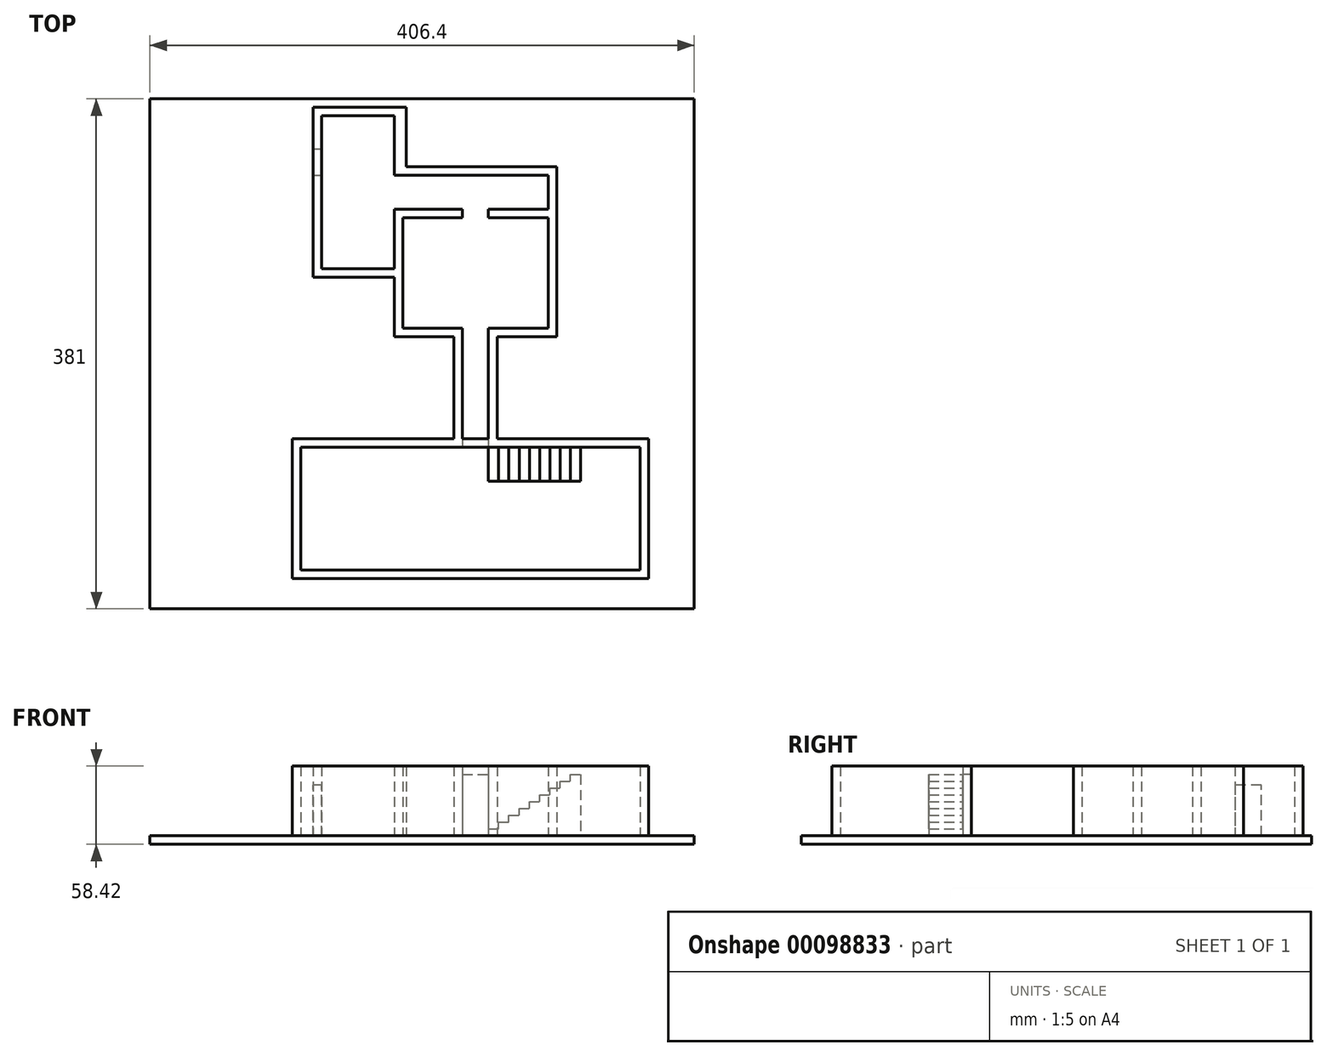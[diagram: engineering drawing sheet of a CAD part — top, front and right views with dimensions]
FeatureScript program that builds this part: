
annotation { "Feature Type Name" : "Feature", "Feature Type Description" : "" }
export const myFeature = defineFeature(function(context is Context, id is Id, definition is map)
    precondition{}
    {
        {
            var Q0;
            Q0=qCreatedBy(makeId("Top.planeOp"),FACE);
            var sketch = newSketch(context, id + "F0", { "sketchPlane" : qUnion([Q0])});
            skLineSegment(sketch, "E0.bottom", {"start": v(-211.11, 667.88) * mm, "end": v(195.29, 667.88) * mm});
            skLineSegment(sketch, "E0.top", {"start": v(-211.11, 286.88) * mm, "end": v(195.29, 286.88) * mm});
            skLineSegment(sketch, "E0.left", {"start": v(-211.11, 667.88) * mm, "end": v(-211.11, 286.88) * mm});
            skLineSegment(sketch, "E0.right", {"start": v(195.29, 667.88) * mm, "end": v(195.29, 286.88) * mm});
            skSolve(sketch);
        }
        {
            var Q0;
            Q0 = qSketchRegion(id + "F0", true);
            extrude(context, id + "F1", {"entities" : qUnion([Q0]), "oppositeDirection" : true, "depth" : 6.35 * mm});
        }
        {
            var Q0;
            Q0=makeQuery(id+"F1.opExtrude","CAP_FACE",FACE,{"disambiguationData":[OSD([sQuery(id+"F0.wireOp",EDGE,"E0.bottom"),sQuery(id+"F0.wireOp",EDGE,"E0.top"),sQuery(id+"F0.wireOp",EDGE,"E0.left"),sQuery(id+"F0.wireOp",EDGE,"E0.right")])],"isStart":true});
            var sketch = newSketch(context, id + "F2", { "sketchPlane" : qUnion([Q0])});
            skLineSegment(sketch, "E1", {"start": v(-89.15, 534.53) * mm, "end": v(-89.15, 661.53) * mm});
            skLineSegment(sketch, "E2", {"start": v(-89.15, 661.53) * mm, "end": v(-19.87, 661.53) * mm});
            skLineSegment(sketch, "E3", {"start": v(-28.62, 585.33) * mm, "end": v(-28.62, 540.88) * mm});
            skLineSegment(sketch, "E4", {"start": v(-28.62, 540.88) * mm, "end": v(-82.8, 540.88) * mm});
            skLineSegment(sketch, "E5", {"start": v(-82.8, 540.88) * mm, "end": v(-82.8, 655.18) * mm});
            skLineSegment(sketch, "E6", {"start": v(-82.8, 655.18) * mm, "end": v(-28.62, 655.18) * mm});
            skLineSegment(sketch, "E7", {"start": v(-28.62, 655.18) * mm, "end": v(-28.62, 610.73) * mm});
            skLineSegment(sketch, "E8", {"start": v(22.18, 585.33) * mm, "end": v(-28.62, 585.33) * mm});
            skLineSegment(sketch, "E9", {"start": v(-89.15, 534.53) * mm, "end": v(-28.62, 534.53) * mm});
            skLineSegment(sketch, "E10", {"start": v(-28.62, 534.53) * mm, "end": v(-28.62, 490.05) * mm});
            skLineSegment(sketch, "E11", {"start": v(-22.27, 496.4) * mm, "end": v(-22.27, 578.98) * mm});
            skLineSegment(sketch, "E12", {"start": v(-22.27, 578.98) * mm, "end": v(22.18, 578.98) * mm});
            skLineSegment(sketch, "E13", {"start": v(22.18, 578.98) * mm, "end": v(22.18, 585.33) * mm});
            skLineSegment(sketch, "E14", {"start": v(-19.87, 661.53) * mm, "end": v(-19.87, 617.08) * mm});
            skLineSegment(sketch, "E15", {"start": v(41.7, 578.98) * mm, "end": v(41.7, 585.33) * mm});
            skLineSegment(sketch, "E16", {"start": v(92.5, 585.33) * mm, "end": v(92.5, 490.05) * mm});
            skLineSegment(sketch, "E17", {"start": v(86.16, 496.41) * mm, "end": v(86.16, 578.98) * mm});
            skLineSegment(sketch, "E18", {"start": v(86.16, 578.98) * mm, "end": v(41.7, 578.98) * mm});
            skLineSegment(sketch, "E19", {"start": v(92.5, 617.08) * mm, "end": v(-19.87, 617.08) * mm});
            skLineSegment(sketch, "E20", {"start": v(92.5, 610.73) * mm, "end": v(92.5, 585.33) * mm});
            skLineSegment(sketch, "E21", {"start": v(92.5, 617.08) * mm, "end": v(92.5, 610.73) * mm});
            skLineSegment(sketch, "E22", {"start": v(86.16, 610.73) * mm, "end": v(86.16, 585.33) * mm});
            skLineSegment(sketch, "E23", {"start": v(86.16, 585.33) * mm, "end": v(41.7, 585.33) * mm});
            skLineSegment(sketch, "E24", {"start": v(86.16, 610.73) * mm, "end": v(-28.62, 610.73) * mm});
            skLineSegment(sketch, "E25", {"start": v(22.18, 490.05) * mm, "end": v(22.18, 496.4) * mm});
            skLineSegment(sketch, "E26", {"start": v(22.18, 496.4) * mm, "end": v(-22.27, 496.4) * mm});
            skLineSegment(sketch, "E27", {"start": v(86.16, 496.41) * mm, "end": v(41.7, 496.41) * mm});
            skLineSegment(sketch, "E28", {"start": v(41.7, 496.41) * mm, "end": v(41.7, 490.05) * mm});
            skLineSegment(sketch, "E29", {"start": v(15.83, 490.05) * mm, "end": v(15.83, 413.85) * mm});
            skLineSegment(sketch, "E30", {"start": v(-28.62, 490.05) * mm, "end": v(15.83, 490.05) * mm});
            skLineSegment(sketch, "E31", {"start": v(48.06, 413.85) * mm, "end": v(48.06, 490.05) * mm});
            skLineSegment(sketch, "E32", {"start": v(48.06, 490.05) * mm, "end": v(92.5, 490.05) * mm});
            skLineSegment(sketch, "E33", {"start": v(22.18, 490.05) * mm, "end": v(22.18, 407.5) * mm});
            skLineSegment(sketch, "E34", {"start": v(41.7, 490.05) * mm, "end": v(41.7, 407.5) * mm});
            skLineSegment(sketch, "E35", {"start": v(41.7, 407.5) * mm, "end": v(154.83, 407.5) * mm});
            skLineSegment(sketch, "E36", {"start": v(154.83, 407.5) * mm, "end": v(154.83, 315.97) * mm});
            skLineSegment(sketch, "E37", {"start": v(154.83, 315.97) * mm, "end": v(-98.59, 315.97) * mm});
            skLineSegment(sketch, "E38", {"start": v(-98.59, 315.97) * mm, "end": v(-98.59, 407.5) * mm});
            skLineSegment(sketch, "E39", {"start": v(-98.59, 407.5) * mm, "end": v(22.18, 407.5) * mm});
            skLineSegment(sketch, "E40", {"start": v(15.83, 413.85) * mm, "end": v(-104.94, 413.85) * mm});
            skLineSegment(sketch, "E41", {"start": v(-104.94, 413.85) * mm, "end": v(-104.94, 309.62) * mm});
            skLineSegment(sketch, "E42", {"start": v(-104.94, 309.62) * mm, "end": v(161.18, 309.62) * mm});
            skLineSegment(sketch, "E43", {"start": v(161.18, 309.62) * mm, "end": v(161.18, 413.85) * mm});
            skLineSegment(sketch, "E44", {"start": v(161.18, 413.85) * mm, "end": v(48.06, 413.85) * mm});
            skSolve(sketch);
        }
        {
            var Q0;
            Q0 = qSketchRegion(id + "F2", true);
            extrude(context, id + "F3", {"entities" : qUnion([Q0]), "operationType" : NewBodyOperationType.ADD, "depth" : 52.07 * mm});
        }
        {
            var Q0;
            Q0=makeQuery(id+"F3.opExtrude","SWEPT_FACE",FACE,{"disambiguationData":[OSD([sQuery(id+"F2.wireOp",EDGE,"E1")])]});
            var sketch = newSketch(context, id + "F4", { "sketchPlane" : qUnion([Q0])});
            skLineSegment(sketch, "E45", {"start": v(-630.27, 0) * mm, "end": v(-630.27, 38.04) * mm});
            skLineSegment(sketch, "E46", {"start": v(-630.27, 38.04) * mm, "end": v(-610.57, 38.04) * mm});
            skLineSegment(sketch, "E47", {"start": v(-610.57, 38.04) * mm, "end": v(-610.57, 0) * mm});
            skLineSegment(sketch, "E48", {"start": v(-610.57, 0) * mm, "end": v(-630.27, 0) * mm});
            skSolve(sketch);
        }
        {
            var Q0;
            Q0 = qSketchRegion(id + "F4", true);
            extrude(context, id + "F5", {"entities" : qUnion([Q0]), "operationType" : NewBodyOperationType.REMOVE, "oppositeDirection" : true, "depth" : 25.4 * mm});
        }
        {
            var Q0;
            Q0=makeQuery(id+"F3.opExtrude","SWEPT_FACE",FACE,{"disambiguationData":[OSD([sQuery(id+"F2.wireOp",EDGE,"E35")])]});
            var sketch = newSketch(context, id + "F6", { "sketchPlane" : qUnion([Q0])});
            skLineSegment(sketch, "E49", {"start": v(41.7, 0) * mm, "end": v(41.7, 5.08) * mm});
            skLineSegment(sketch, "E50", {"start": v(41.7, 5.08) * mm, "end": v(49.33, 5.08) * mm});
            skLineSegment(sketch, "E51", {"start": v(49.33, 5.08) * mm, "end": v(49.33, 10.16) * mm});
            skLineSegment(sketch, "E52", {"start": v(49.33, 10.16) * mm, "end": v(56.95, 10.16) * mm});
            skLineSegment(sketch, "E53", {"start": v(56.95, 10.16) * mm, "end": v(56.95, 15.24) * mm});
            skLineSegment(sketch, "E54", {"start": v(56.95, 15.24) * mm, "end": v(64.57, 15.24) * mm});
            skLineSegment(sketch, "E55", {"start": v(64.57, 15.24) * mm, "end": v(64.57, 20.32) * mm});
            skLineSegment(sketch, "E56", {"start": v(64.57, 20.32) * mm, "end": v(72.19, 20.32) * mm});
            skLineSegment(sketch, "E57", {"start": v(72.19, 20.32) * mm, "end": v(72.19, 25.4) * mm});
            skLineSegment(sketch, "E58", {"start": v(72.19, 25.4) * mm, "end": v(79.8, 25.4) * mm});
            skLineSegment(sketch, "E59", {"start": v(79.8, 25.4) * mm, "end": v(79.8, 30.48) * mm});
            skLineSegment(sketch, "E60", {"start": v(79.8, 30.48) * mm, "end": v(87.43, 30.48) * mm});
            skLineSegment(sketch, "E61", {"start": v(87.43, 30.48) * mm, "end": v(87.43, 35.56) * mm});
            skLineSegment(sketch, "E62", {"start": v(87.43, 35.56) * mm, "end": v(95.05, 35.56) * mm});
            skLineSegment(sketch, "E63", {"start": v(95.05, 35.56) * mm, "end": v(95.05, 40.64) * mm});
            skLineSegment(sketch, "E64", {"start": v(95.05, 40.64) * mm, "end": v(102.67, 40.64) * mm});
            skLineSegment(sketch, "E65", {"start": v(102.67, 40.64) * mm, "end": v(102.67, 45.72) * mm});
            skLineSegment(sketch, "E66", {"start": v(102.67, 45.72) * mm, "end": v(110.29, 45.72) * mm});
            skLineSegment(sketch, "E67", {"start": v(110.29, 45.72) * mm, "end": v(110.29, 0) * mm});
            skLineSegment(sketch, "E68", {"start": v(110.29, 0) * mm, "end": v(41.7, 0) * mm});
            skSolve(sketch);
        }
        {
            var Q0;
            Q0 = qSketchRegion(id + "F6", true);
            extrude(context, id + "F7", {"entities" : qUnion([Q0]), "operationType" : NewBodyOperationType.ADD, "depth" : 25.4 * mm});
        }
        {
            var Q0;
            Q0=makeQuery(id+"F3.opExtrude","CAP_FACE",FACE,{"disambiguationData":[OSD([sQuery(id+"F2.wireOp",EDGE,"E1"),sQuery(id+"F2.wireOp",EDGE,"E2"),sQuery(id+"F2.wireOp",EDGE,"E3"),sQuery(id+"F2.wireOp",EDGE,"E4"),sQuery(id+"F2.wireOp",EDGE,"E5"),sQuery(id+"F2.wireOp",EDGE,"E6"),sQuery(id+"F2.wireOp",EDGE,"E7"),sQuery(id+"F2.wireOp",EDGE,"E8"),sQuery(id+"F2.wireOp",EDGE,"E9"),sQuery(id+"F2.wireOp",EDGE,"E10"),sQuery(id+"F2.wireOp",EDGE,"E11"),sQuery(id+"F2.wireOp",EDGE,"E12"),sQuery(id+"F2.wireOp",EDGE,"E13"),sQuery(id+"F2.wireOp",EDGE,"E14"),sQuery(id+"F2.wireOp",EDGE,"E15"),sQuery(id+"F2.wireOp",EDGE,"E16"),sQuery(id+"F2.wireOp",EDGE,"E17"),sQuery(id+"F2.wireOp",EDGE,"E18"),sQuery(id+"F2.wireOp",EDGE,"E19"),sQuery(id+"F2.wireOp",EDGE,"E20"),sQuery(id+"F2.wireOp",EDGE,"E21"),sQuery(id+"F2.wireOp",EDGE,"E22"),sQuery(id+"F2.wireOp",EDGE,"E23"),sQuery(id+"F2.wireOp",EDGE,"E24"),sQuery(id+"F2.wireOp",EDGE,"E25"),sQuery(id+"F2.wireOp",EDGE,"E26"),sQuery(id+"F2.wireOp",EDGE,"E27"),sQuery(id+"F2.wireOp",EDGE,"E28"),sQuery(id+"F2.wireOp",EDGE,"E29"),sQuery(id+"F2.wireOp",EDGE,"E30"),sQuery(id+"F2.wireOp",EDGE,"E31"),sQuery(id+"F2.wireOp",EDGE,"E32"),sQuery(id+"F2.wireOp",EDGE,"E33"),sQuery(id+"F2.wireOp",EDGE,"E34"),sQuery(id+"F2.wireOp",EDGE,"E35"),sQuery(id+"F2.wireOp",EDGE,"E36"),sQuery(id+"F2.wireOp",EDGE,"E37"),sQuery(id+"F2.wireOp",EDGE,"E38"),sQuery(id+"F2.wireOp",EDGE,"E39"),sQuery(id+"F2.wireOp",EDGE,"E40"),sQuery(id+"F2.wireOp",EDGE,"E41"),sQuery(id+"F2.wireOp",EDGE,"E42"),sQuery(id+"F2.wireOp",EDGE,"E43"),sQuery(id+"F2.wireOp",EDGE,"E44")])],"isStart":false});
            var sketch = newSketch(context, id + "F8", { "sketchPlane" : qUnion([Q0])});
            skLineSegment(sketch, "E69.bottom", {"start": v(-104.94, 413.85) * mm, "end": v(161.18, 413.85) * mm});
            skLineSegment(sketch, "E69.top", {"start": v(-104.94, 309.62) * mm, "end": v(161.18, 309.62) * mm});
            skLineSegment(sketch, "E69.left", {"start": v(-104.94, 413.85) * mm, "end": v(-104.94, 309.62) * mm});
            skLineSegment(sketch, "E69.right", {"start": v(161.18, 413.85) * mm, "end": v(161.18, 309.62) * mm});
            skLineSegment(sketch, "E70.bottom", {"start": v(-98.59, 407.5) * mm, "end": v(154.83, 407.5) * mm});
            skLineSegment(sketch, "E70.top", {"start": v(-98.59, 315.97) * mm, "end": v(154.83, 315.97) * mm});
            skLineSegment(sketch, "E70.left", {"start": v(-98.59, 407.5) * mm, "end": v(-98.59, 315.97) * mm});
            skLineSegment(sketch, "E70.right", {"start": v(154.83, 407.5) * mm, "end": v(154.83, 315.97) * mm});
            skSolve(sketch);
        }
        {
            var Q0;
            Q0 = qSketchRegion(id + "F8", true);
            extrude(context, id + "F9", {"entities" : qUnion([Q0]), "operationType" : NewBodyOperationType.ADD, "oppositeDirection" : true, "depth" : 6.35 * mm});
        }
    });
